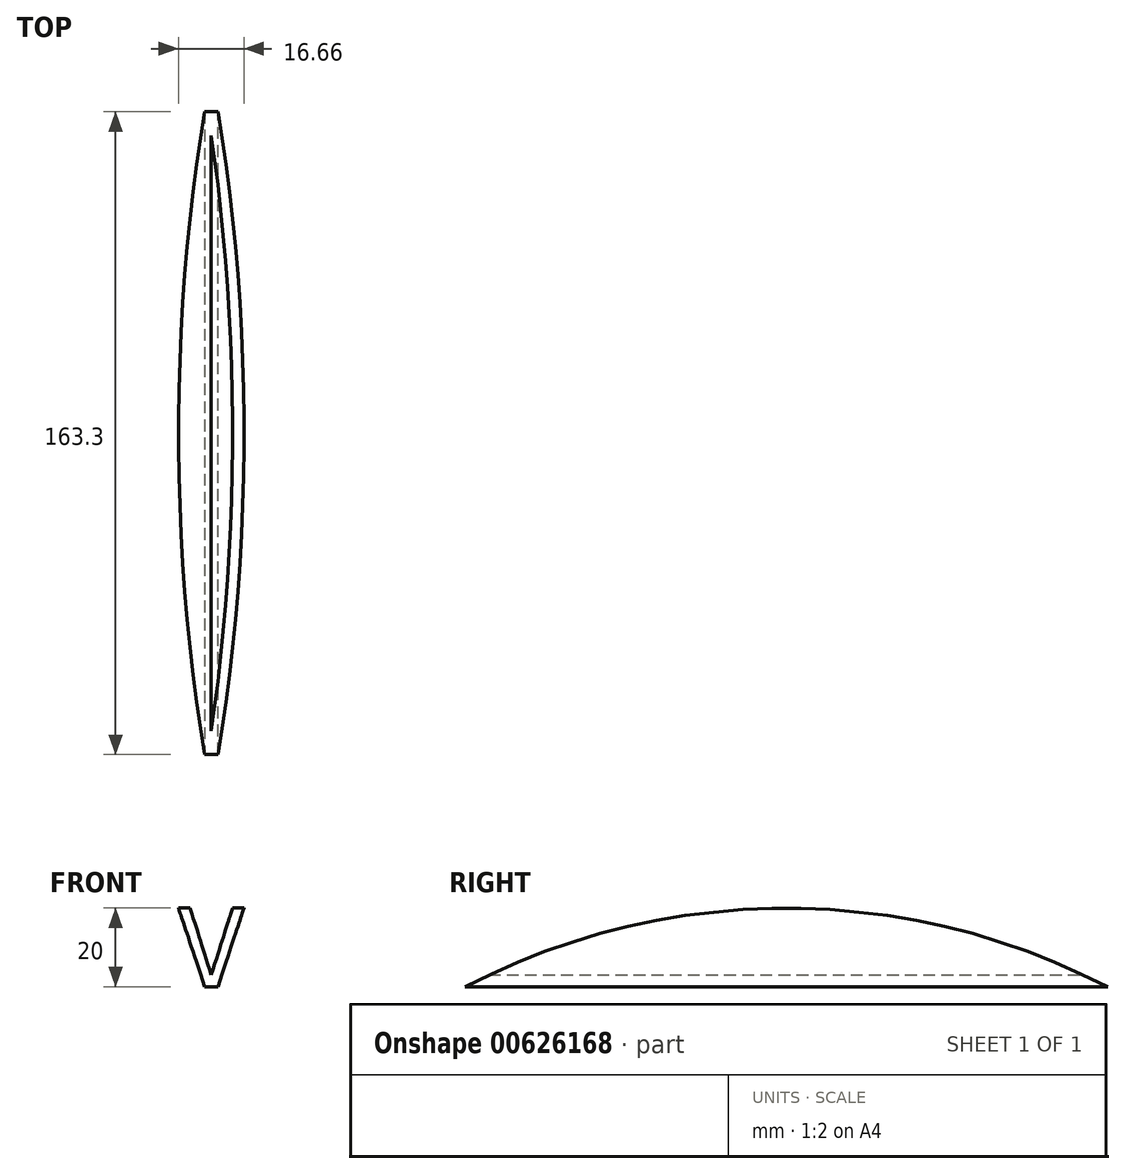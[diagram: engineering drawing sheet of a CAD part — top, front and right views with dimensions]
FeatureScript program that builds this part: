
annotation { "Feature Type Name" : "Feature", "Feature Type Description" : "" }
export const myFeature = defineFeature(function(context is Context, id is Id, definition is map)
    precondition{}
    {
        {
            var Q0;
            Q0=qCreatedBy(makeId("Front.planeOp"),FACE);
            var sketch = newSketch(context, id + "F0", { "sketchPlane" : qUnion([Q0])});
            skLineSegment(sketch, "E0", {"start": v(0, 0) * mm, "end": v(10, 30) * mm});
            skLineSegment(sketch, "E1", {"start": v(10, 30) * mm, "end": v(-10, 30) * mm});
            skLineSegment(sketch, "E2", {"start": v(-10, 30) * mm, "end": v(0, 0) * mm});
            skSolve(sketch);
        }
        {
            var Q0;
            Q0=makeQuery(id+"F0.imprint","IMPRINT",FACE,{"disambiguationData":[TD([[makeQuery(id+"F0.imprint","IMPRINT",EDGE,{"derivedFrom":sQuery(id+"F0.wireOp",EDGE,"E0")}),1.0]])]});
            extrude(context, id + "F1", {"entities" : qUnion([Q0]), "depth" : 200 * mm, "offsetDistance" : 25 * mm});
        }
        {
            var Q0;
            Q0=qCreatedBy(makeId("Right.planeOp"),FACE);
            var sketch = newSketch(context, id + "F2", { "sketchPlane" : qUnion([Q0])});
            skLineSegment(sketch, "E3", {"start": v(0, 0) * mm, "end": v(0, 30) * mm});
            skLineSegment(sketch, "E4", {"start": v(0, 30) * mm, "end": v(-200, 30) * mm});
            skLineSegment(sketch, "E5", {"start": v(-200, 30) * mm, "end": v(-200, 0) * mm});
            skArc(sketch, "E6", {"start": v(0, 0) * mm, "mid": v(-100, 30) * mm, "end": v(-200, 0) * mm});
            skSolve(sketch);
        }
        {
            var Q0;
            Q0 = qSketchRegion(id + "F2", true);
            extrude(context, id + "F3", {"entities" : qUnion([Q0]), "operationType" : NewBodyOperationType.REMOVE, "endBound" : BoundingType.SYMMETRIC, "oppositeDirection" : true, "depth" : 25 * mm, "offsetDistance" : 25 * mm});
        }
        {
            var Q0;
            Q0=qCreatedBy(makeId("Front.planeOp"),FACE);
            var sketch = newSketch(context, id + "F4", { "sketchPlane" : qUnion([Q0])});
            skLineSegment(sketch, "E7", {"start": v(0, 8) * mm, "end": v(-7, 30) * mm});
            skLineSegment(sketch, "E8", {"start": v(-7, 30) * mm, "end": v(7, 30) * mm});
            skLineSegment(sketch, "E9", {"start": v(7, 30) * mm, "end": v(0, 8) * mm});
            skSolve(sketch);
        }
        {
            var Q0;
            Q0 = qSketchRegion(id + "F4", true);
            extrude(context, id + "F5", {"entities" : qUnion([Q0]), "operationType" : NewBodyOperationType.REMOVE, "endBound" : BoundingType.THROUGH_ALL, "depth" : 25 * mm, "offsetDistance" : 25 * mm});
        }
        {
            var Q0;
            Q0=qCreatedBy(makeId("Right.planeOp"),FACE);
            var sketch = newSketch(context, id + "F6", { "sketchPlane" : qUnion([Q0])});
            skLineSegment(sketch, "E10", {"start": v(0, 0) * mm, "end": v(-200, 0) * mm});
            skLineSegment(sketch, "E11", {"start": v(-200, 0) * mm, "end": v(-200, 30) * mm});
            skLineSegment(sketch, "E12", {"start": v(-200, 30) * mm, "end": v(0, 30) * mm});
            skLineSegment(sketch, "E13", {"start": v(0, 30) * mm, "end": v(0, 0) * mm});
            skArc(sketch, "E14", {"start": v(0, 0) * mm, "mid": v(-100, 30) * mm, "end": v(-200, 0) * mm});
            skArc(sketch, "E15.0", {"start": v(-181.65, 5) * mm, "mid": v(-100, 25) * mm, "end": v(-18.35, 5) * mm});
            skLineSegment(sketch, "E15.1", {"start": v(-18.35, 5) * mm, "end": v(-181.65, 5) * mm});
            skSolve(sketch);
        }
        {
            var Q0;
            Q0=makeQuery(id+"F6.imprint","IMPRINT",FACE,{"disambiguationData":[TD([[makeQuery(id+"F6.imprint","IMPRINT",EDGE,{"derivedFrom":sQuery(id+"F6.wireOp",EDGE,"E15.0")}),-1.0]])]});
            extrude(context, id + "F7", {"entities" : qUnion([Q0]), "operationType" : NewBodyOperationType.REMOVE, "endBound" : BoundingType.SYMMETRIC, "oppositeDirection" : true, "depth" : 25 * mm, "offsetDistance" : 25 * mm});
        }
        {
            var Q0;
            Q0=qCreatedBy(makeId("Right.planeOp"),FACE);
            var sketch = newSketch(context, id + "F8", { "sketchPlane" : qUnion([Q0])});
            skLineSegment(sketch, "E16", {"start": v(0, 0) * mm, "end": v(-100, 0) * mm});
            skLineSegment(sketch, "E17", {"start": v(-100, 0) * mm, "end": v(-100, 44.5) * mm});
            skLineSegment(sketch, "E18", {"start": v(0, 3.17) * mm, "end": v(-12.42, 3.17) * mm});
            skLineSegment(sketch, "E19", {"start": v(-12.42, 3.17) * mm, "end": v(-12.42, -5.25) * mm});
            skLineSegment(sketch, "E20", {"start": v(-12.42, -5.25) * mm, "end": v(0, -5.25) * mm});
            skLineSegment(sketch, "E21", {"start": v(0, -5.25) * mm, "end": v(0, 3.17) * mm});
            skLineSegment(sketch, "E22.MirrorCS", {"start": v(-200, 3.17) * mm, "end": v(-187.58, 3.17) * mm});
            skLineSegment(sketch, "E23.MirrorCS", {"start": v(-187.58, 3.17) * mm, "end": v(-187.58, -5.25) * mm});
            skLineSegment(sketch, "E24.MirrorCS", {"start": v(-200, -5.25) * mm, "end": v(-200, 3.17) * mm});
            skLineSegment(sketch, "E25.MirrorCS", {"start": v(-187.58, -5.25) * mm, "end": v(-200, -5.25) * mm});
            skSolve(sketch);
        }
        {
            var Q0;
            {var subQ5=sQuery(id+"F8.wireOp",EDGE,"E20");Q0=makeQuery(id+"F8.imprint","IMPRINT",FACE,{"disambiguationData":[TD([[makeQuery(id+"F8.imprint","IMPRINT",EDGE,{"derivedFrom":subQ5}),1.0]])]});}
            var Q1;
            {var subQ5=sQuery(id+"F8.wireOp",EDGE,"E18");Q1=makeQuery(id+"F8.imprint","IMPRINT",FACE,{"disambiguationData":[TD([[makeQuery(id+"F8.imprint","IMPRINT",EDGE,{"derivedFrom":subQ5}),1.0]])]});}
            var Q2;
            Q2=makeQuery(id+"F8.imprint","IMPRINT",FACE,{"disambiguationData":[TD([[makeQuery(id+"F8.imprint","IMPRINT",EDGE,{"derivedFrom":sQuery(id+"F8.wireOp",EDGE,"E22.MirrorCS")}),-1.0]])]});
            extrude(context, id + "F9", {"entities" : qUnion([Q0, Q1, Q2]), "operationType" : NewBodyOperationType.REMOVE, "endBound" : BoundingType.SYMMETRIC, "oppositeDirection" : true, "depth" : 25 * mm, "offsetDistance" : 25 * mm});
        }
    });
